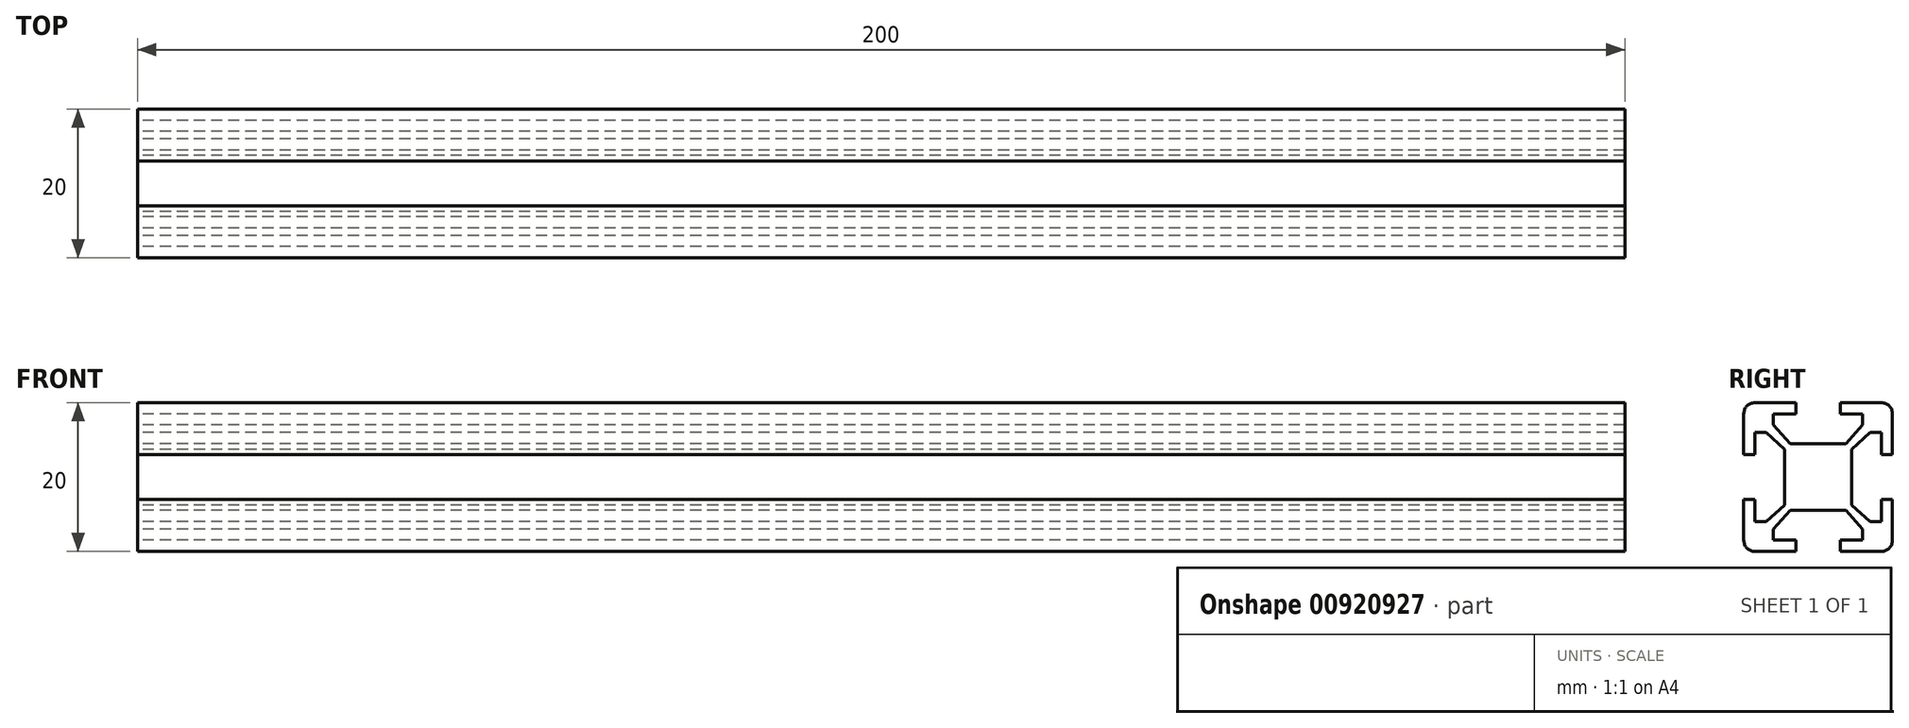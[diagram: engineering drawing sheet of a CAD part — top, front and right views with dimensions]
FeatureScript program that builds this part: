
annotation { "Feature Type Name" : "Feature", "Feature Type Description" : "" }
export const myFeature = defineFeature(function(context is Context, id is Id, definition is map)
    precondition{}
    {
        {
            var Q0;
            Q0=qCreatedBy(makeId("Right.planeOp"),FACE);
            var sketch = newSketch(context, id + "F0", { "sketchPlane" : qUnion([Q0])});
            skLineSegment(sketch, "E0.bottom", {"start": v(8.5, 10) * mm, "end": v(3, 10) * mm});
            skLineSegment(sketch, "E0.top", {"start": v(8.5, -10) * mm, "end": v(-8.5, -10) * mm});
            skLineSegment(sketch, "E0.left", {"start": v(10, 8.5) * mm, "end": v(10, 3) * mm});
            skLineSegment(sketch, "E0.right", {"start": v(-10, 8.5) * mm, "end": v(-10, 3) * mm});
            skPoint(sketch, "E0.middle", {"position": v(0, 0) * mm});
            skPoint(sketch, "E1.visualSharp", {"position": v(-10, 10) * mm});
            skArc(sketch, "E1.filletArc", {"start": v(-8.5, 10) * mm, "mid": v(-9.56, 9.56) * mm, "end": v(-10, 8.5) * mm});
            skPoint(sketch, "E2.visualSharp", {"position": v(10, 10) * mm});
            skArc(sketch, "E2.filletArc", {"start": v(10, 8.5) * mm, "mid": v(9.56, 9.56) * mm, "end": v(8.5, 10) * mm});
            skPoint(sketch, "E3.visualSharp", {"position": v(10, -10) * mm});
            skArc(sketch, "E3.filletArc", {"start": v(8.5, -10) * mm, "mid": v(9.56, -9.56) * mm, "end": v(10, -8.5) * mm});
            skPoint(sketch, "E4.visualSharp", {"position": v(-10, -10) * mm});
            skArc(sketch, "E4.filletArc", {"start": v(-10, -8.5) * mm, "mid": v(-9.56, -9.56) * mm, "end": v(-8.5, -10) * mm});
            skLineSegment(sketch, "E5", {"start": v(-3, 10) * mm, "end": v(-3, 8.5) * mm});
            skLineSegment(sketch, "E6", {"start": v(-3, 8.5) * mm, "end": v(-6, 8.5) * mm});
            skLineSegment(sketch, "E7", {"start": v(-6, 8.5) * mm, "end": v(-6, 7) * mm});
            skLineSegment(sketch, "E8", {"start": v(-6, 7) * mm, "end": v(-3.75, 4.5) * mm});
            skLineSegment(sketch, "E9", {"start": v(-3.75, 4.5) * mm, "end": v(0, 4.5) * mm});
            skLineSegment(sketch, "E10.MirrorCS", {"start": v(3, 10) * mm, "end": v(3, 8.5) * mm});
            skLineSegment(sketch, "E11.MirrorCS", {"start": v(3, 8.5) * mm, "end": v(6, 8.5) * mm});
            skLineSegment(sketch, "E12.MirrorCS", {"start": v(6, 8.5) * mm, "end": v(6, 7) * mm});
            skLineSegment(sketch, "E13.MirrorCS", {"start": v(6, 7) * mm, "end": v(3.75, 4.5) * mm});
            skLineSegment(sketch, "E14.MirrorCS", {"start": v(3.75, 4.5) * mm, "end": v(0, 4.5) * mm});
            skLineSegment(sketch, "E15.trimOffspring", {"start": v(-3, 10) * mm, "end": v(-8.5, 10) * mm});
            skLineSegment(sketch, "E16.1.0", {"start": v(-8.5, -3) * mm, "end": v(-8.5, -6) * mm});
            skLineSegment(sketch, "E16.1.1", {"start": v(-8.5, -6) * mm, "end": v(-7, -6) * mm});
            skLineSegment(sketch, "E16.1.2", {"start": v(-7, -6) * mm, "end": v(-4.5, -3.75) * mm});
            skLineSegment(sketch, "E16.1.3", {"start": v(-4.5, -3.75) * mm, "end": v(-4.5, 0) * mm});
            skLineSegment(sketch, "E16.1.4", {"start": v(-4.5, 3.75) * mm, "end": v(-4.5, 0) * mm});
            skLineSegment(sketch, "E16.1.5", {"start": v(-7, 6) * mm, "end": v(-4.5, 3.75) * mm});
            skLineSegment(sketch, "E16.1.6", {"start": v(-8.5, 6) * mm, "end": v(-7, 6) * mm});
            skLineSegment(sketch, "E16.1.7", {"start": v(-8.5, 3) * mm, "end": v(-8.5, 6) * mm});
            skLineSegment(sketch, "E16.1.8", {"start": v(-10, 3) * mm, "end": v(-8.5, 3) * mm});
            skLineSegment(sketch, "E16.1.9", {"start": v(-10, -3) * mm, "end": v(-8.5, -3) * mm});
            skLineSegment(sketch, "E16.2.0", {"start": v(3, -8.5) * mm, "end": v(6, -8.5) * mm});
            skLineSegment(sketch, "E16.2.1", {"start": v(6, -8.5) * mm, "end": v(6, -7) * mm});
            skLineSegment(sketch, "E16.2.2", {"start": v(6, -7) * mm, "end": v(3.75, -4.5) * mm});
            skLineSegment(sketch, "E16.2.3", {"start": v(3.75, -4.5) * mm, "end": v(0, -4.5) * mm});
            skLineSegment(sketch, "E16.2.4", {"start": v(-3.75, -4.5) * mm, "end": v(0, -4.5) * mm});
            skLineSegment(sketch, "E16.2.5", {"start": v(-6, -7) * mm, "end": v(-3.75, -4.5) * mm});
            skLineSegment(sketch, "E16.2.6", {"start": v(-6, -8.5) * mm, "end": v(-6, -7) * mm});
            skLineSegment(sketch, "E16.2.7", {"start": v(-3, -8.5) * mm, "end": v(-6, -8.5) * mm});
            skLineSegment(sketch, "E16.2.8", {"start": v(-3, -10) * mm, "end": v(-3, -8.5) * mm});
            skLineSegment(sketch, "E16.2.9", {"start": v(3, -10) * mm, "end": v(3, -8.5) * mm});
            skLineSegment(sketch, "E16.3.0", {"start": v(8.5, 3) * mm, "end": v(8.5, 6) * mm});
            skLineSegment(sketch, "E16.3.1", {"start": v(8.5, 6) * mm, "end": v(7, 6) * mm});
            skLineSegment(sketch, "E16.3.2", {"start": v(7, 6) * mm, "end": v(4.5, 3.75) * mm});
            skLineSegment(sketch, "E16.3.3", {"start": v(4.5, 3.75) * mm, "end": v(4.5, 0) * mm});
            skLineSegment(sketch, "E16.3.4", {"start": v(4.5, -3.75) * mm, "end": v(4.5, 0) * mm});
            skLineSegment(sketch, "E16.3.5", {"start": v(7, -6) * mm, "end": v(4.5, -3.75) * mm});
            skLineSegment(sketch, "E16.3.6", {"start": v(8.5, -6) * mm, "end": v(7, -6) * mm});
            skLineSegment(sketch, "E16.3.7", {"start": v(8.5, -3) * mm, "end": v(8.5, -6) * mm});
            skLineSegment(sketch, "E16.3.8", {"start": v(10, -3) * mm, "end": v(8.5, -3) * mm});
            skLineSegment(sketch, "E16.3.9", {"start": v(10, 3) * mm, "end": v(8.5, 3) * mm});
            skLineSegment(sketch, "E17.trimOffspring", {"start": v(-10, -3) * mm, "end": v(-10, -8.5) * mm});
            skLineSegment(sketch, "E18.trimOffspring", {"start": v(10, -3) * mm, "end": v(10, -8.5) * mm});
            skSolve(sketch);
        }
        {
            var Q0;
            Q0=makeQuery(id+"F0.imprint","IMPRINT",FACE,{"disambiguationData":[TD([[makeQuery(id+"F0.imprint","IMPRINT",EDGE,{"derivedFrom":sQuery(id+"F0.wireOp",EDGE,"E0.bottom")}),1.0]])]});
            extrude(context, id + "F1", {"entities" : qUnion([Q0]), "depth" : 200 * mm, "offsetDistance" : 25 * mm});
        }
    });
